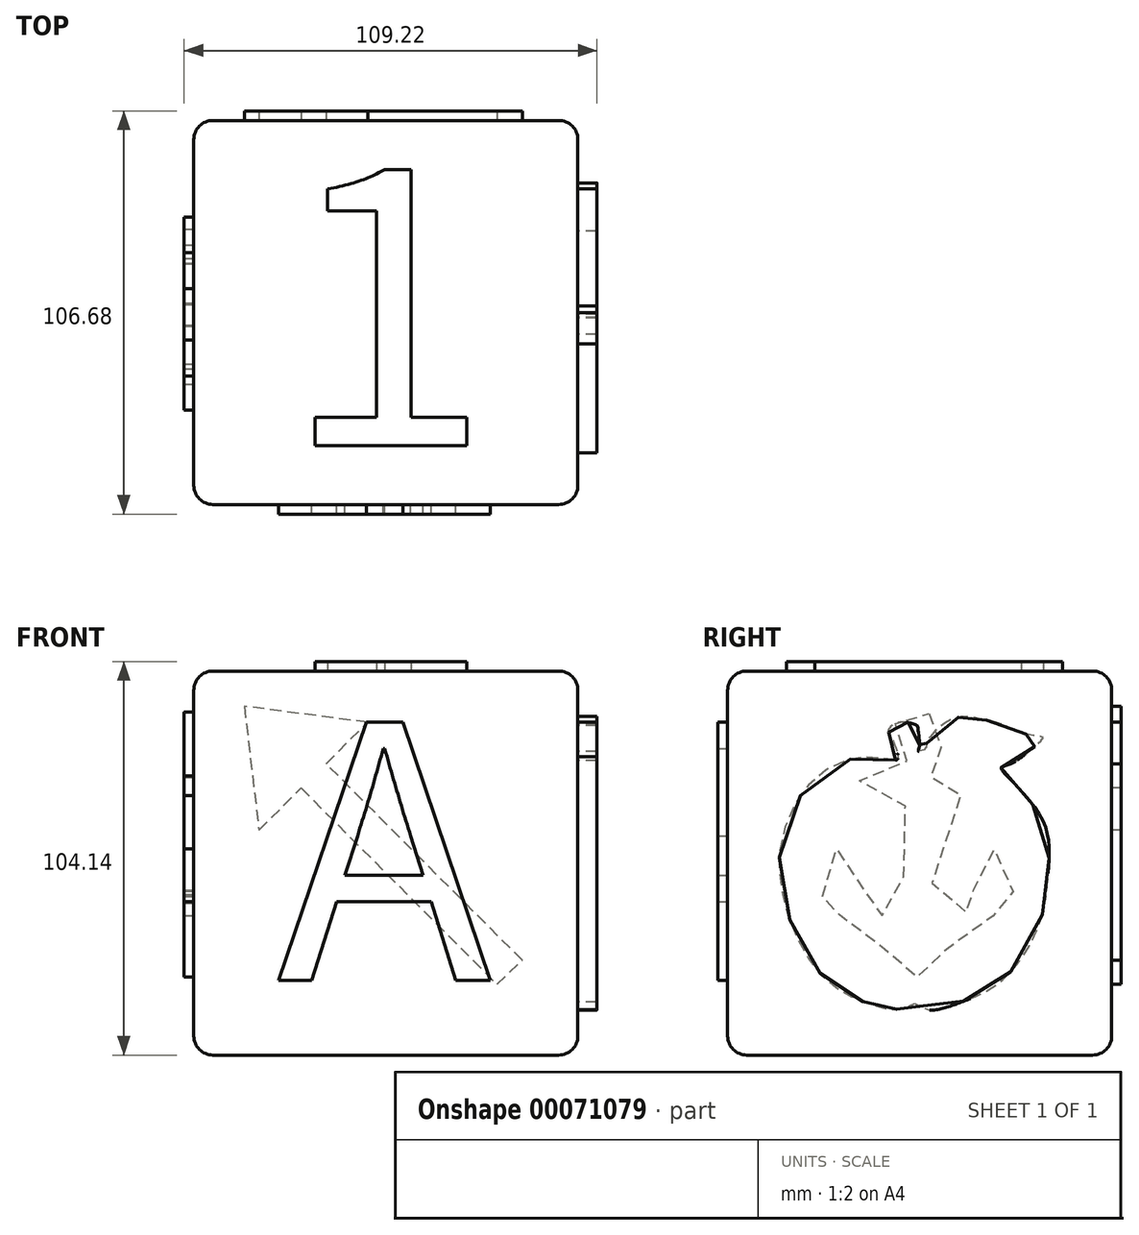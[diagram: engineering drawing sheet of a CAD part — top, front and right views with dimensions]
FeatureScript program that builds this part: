
annotation { "Feature Type Name" : "Feature", "Feature Type Description" : "" }
export const myFeature = defineFeature(function(context is Context, id is Id, definition is map)
    precondition{}
    {
        {
            var Q0;
            Q0=qCreatedBy(makeId("Top.planeOp"),FACE);
            var sketch = newSketch(context, id + "F0", { "sketchPlane" : qUnion([Q0])});
            skLineSegment(sketch, "E0.bottom", {"start": v(-60.77, 32.05) * mm, "end": v(40.83, 32.05) * mm});
            skLineSegment(sketch, "E0.top", {"start": v(-60.77, -69.55) * mm, "end": v(40.83, -69.55) * mm});
            skLineSegment(sketch, "E0.left", {"start": v(-60.77, 32.05) * mm, "end": v(-60.77, -69.55) * mm});
            skLineSegment(sketch, "E0.right", {"start": v(40.83, 32.05) * mm, "end": v(40.83, -69.55) * mm});
            skSolve(sketch);
        }
        {
            var Q0;
            Q0=makeQuery(id+"F0.imprint","IMPRINT",FACE,{"disambiguationData":[TD([[makeQuery(id+"F0.imprint","IMPRINT",EDGE,{"derivedFrom":sQuery(id+"F0.wireOp",EDGE,"E0.bottom")}),-1.0]])]});
            extrude(context, id + "F1", {"entities" : qUnion([Q0]), "depth" : 101.6 * mm});
        }
        {
            var Q0;
            Q0=makeQuery(id+"F1.opExtrude","CAP_EDGE",EDGE,{"disambiguationData":[OSD([sQuery(id+"F0.wireOp",EDGE,"E0.top")])],"isStart":false});
            var Q1;
            Q1=makeQuery(id+"F1.opExtrude","CAP_EDGE",EDGE,{"disambiguationData":[OSD([sQuery(id+"F0.wireOp",EDGE,"E0.right")])],"isStart":false});
            var Q2;
            Q2=makeQuery(id+"F1.opExtrude","CAP_EDGE",EDGE,{"disambiguationData":[OSD([sQuery(id+"F0.wireOp",EDGE,"E0.bottom")])],"isStart":false});
            var Q3;
            Q3=makeQuery(id+"F1.opExtrude","CAP_EDGE",EDGE,{"disambiguationData":[OSD([sQuery(id+"F0.wireOp",EDGE,"E0.left")])],"isStart":false});
            var Q4;
            Q4=makeQuery(id+"F1.opExtrude","SWEPT_EDGE",EDGE,{"disambiguationData":[OSD([sQuery(id+"F0.wireOp",EDGE,"E0.top"),sQuery(id+"F0.wireOp",EDGE,"E0.right")])]});
            var Q5;
            Q5=makeQuery(id+"F1.opExtrude","CAP_EDGE",EDGE,{"disambiguationData":[OSD([sQuery(id+"F0.wireOp",EDGE,"E0.right")])],"isStart":true});
            var Q6;
            Q6=makeQuery(id+"F1.opExtrude","SWEPT_EDGE",EDGE,{"disambiguationData":[OSD([sQuery(id+"F0.wireOp",EDGE,"E0.bottom"),sQuery(id+"F0.wireOp",EDGE,"E0.right")])]});
            var Q7;
            Q7=makeQuery(id+"F1.opExtrude","SWEPT_EDGE",EDGE,{"disambiguationData":[OSD([sQuery(id+"F0.wireOp",EDGE,"E0.top"),sQuery(id+"F0.wireOp",EDGE,"E0.left")])]});
            var Q8;
            Q8=makeQuery(id+"F1.opExtrude","CAP_EDGE",EDGE,{"disambiguationData":[OSD([sQuery(id+"F0.wireOp",EDGE,"E0.top")])],"isStart":true});
            var Q9;
            Q9=makeQuery(id+"F1.opExtrude","SWEPT_EDGE",EDGE,{"disambiguationData":[OSD([sQuery(id+"F0.wireOp",EDGE,"E0.bottom"),sQuery(id+"F0.wireOp",EDGE,"E0.left")])]});
            var Q10;
            Q10=makeQuery(id+"F1.opExtrude","CAP_EDGE",EDGE,{"disambiguationData":[OSD([sQuery(id+"F0.wireOp",EDGE,"E0.bottom")])],"isStart":true});
            var Q11;
            Q11=makeQuery(id+"F1.opExtrude","CAP_EDGE",EDGE,{"disambiguationData":[OSD([sQuery(id+"F0.wireOp",EDGE,"E0.left")])],"isStart":true});
            fillet(context, id + "F2", {"entities" : qUnion([Q0, Q1, Q2, Q3, Q4, Q5, Q6, Q7, Q8, Q9, Q10, Q11]), "radius" : 5.08 * mm, "tangentPropagation" : true, "allowEdgeOverflow" : false});
        }
        {
            var Q0;
            Q0=makeQuery(id+"F1.opExtrude","SWEPT_FACE",FACE,{"disambiguationData":[OSD([sQuery(id+"F0.wireOp",EDGE,"E0.right")])]});
            var sketch = newSketch(context, id + "F3", { "sketchPlane" : qUnion([Q0])});
            skFitSpline(sketch, "E1", {"points": [v(-25.17, 78) * mm, v(-32.49, 78.89) * mm, v(-46.6, 73.07) * mm, v(-55.41, 56.14) * mm, v(-54.09, 38.68) * mm, v(-46.33, 23) * mm, v(-36.9, 15.58) * mm, v(-28.43, 12.41) * mm, v(-25.52, 12.06) * mm, v(-20.06, 13.65) * mm, v(-20.15, 14) * mm, v(-17.68, 12.23) * mm, v(-8.5, 13.73) * mm, v(3.13, 19.9) * mm, v(13.18, 35.51) * mm, v(15.38, 50.41) * mm, v(13.35, 63.02) * mm, v(3.3, 75) * mm, v(2.86, 76.15) * mm, v(5.68, 77.21) * mm, v(13.8, 83.74) * mm, v(13.88, 84.09) * mm, v(9.65, 84.88) * mm, v(1.45, 88.06) * mm, v(-2.78, 88.94) * mm, v(-5.78, 89.62) * mm, v(-11.68, 88.15) * mm, v(-16.97, 82.41) * mm, v(-17.24, 80.92) * mm, v(-19.09, 80.39) * mm, v(-18.91, 81.18) * mm, v(-19.44, 87.26) * mm, v(-19.53, 87.26) * mm, v(-21.56, 87.97) * mm, v(-25.61, 87.53) * mm, v(-27.02, 85.94) * mm, v(-26.76, 85.06) * mm, v(-24.47, 78.98) * mm, v(-25.17, 78) * mm]});
            skSolve(sketch);
        }
        {
            var Q0;
            Q0 = qSketchRegion(id + "F3", true);
            extrude(context, id + "F4", {"entities" : qUnion([Q0]), "operationType" : NewBodyOperationType.ADD, "depth" : 5.08 * mm});
        }
        {
            var Q0;
            Q0=makeQuery(id+"F1.opExtrude","SWEPT_FACE",FACE,{"disambiguationData":[OSD([sQuery(id+"F0.wireOp",EDGE,"E0.left")])]});
            var sketch = newSketch(context, id + "F5", { "sketchPlane" : qUnion([Q0])});
            skPoint(sketch, "E2.107.internal.snap0", {"position": v(19.07, 20.61) * mm});
            skFitSpline(sketch, "E2", {"points": [v(16.32, 90.34) * mm, v(14.88, 89.39) * mm, v(13.13, 86.96) * mm, v(12.61, 85.53) * mm, v(12.54, 83.61) * mm, v(12.81, 82.22) * mm, v(13.73, 80.55) * mm, v(14.93, 79.2) * mm, v(16.05, 78.43) * mm, v(16.56, 78.15) * mm, v(16.56, 77.84) * mm, v(16.45, 73.77) * mm, v(16.4, 73.7) * mm, v(3.25, 73.66) * mm, v(2.93, 73.62) * mm, v(5.8, 69.12) * mm, v(5.8, 68.92) * mm, v(16.05, 68.75) * mm, v(16.17, 68.71) * mm, v(15.42, 45.25) * mm, v(13.07, 38.64) * mm, v(10.72, 37.33) * mm, v(9.48, 36.93) * mm, v(7.01, 37.5) * mm, v(3.42, 40.24) * mm, v(1.75, 42.4) * mm, v(1.07, 43.27) * mm, v(1, 43.59) * mm, v(4.06, 43.59) * mm, v(4.5, 43.75) * mm, v(3.22, 45.06) * mm, v(1.35, 48.1) * mm, v(0, 51.48) * mm, v(-0.89, 53.47) * mm, v(-1.09, 54.86) * mm, v(-2.16, 53.27) * mm, v(-4.12, 49.77) * mm, v(-5.35, 46.58) * mm, v(-6.03, 42.64) * mm, v(-6.42, 40.29) * mm, v(-6.1, 40.49) * mm, v(-3.31, 42.56) * mm, v(-3.27, 42.28) * mm, v(-0.96, 37.3) * mm, v(2.07, 33.47) * mm, v(6.06, 30.56) * mm, v(9.73, 28.69) * mm, v(12.8, 27.45) * mm, v(15.5, 25.54) * mm, v(16.98, 24.46) * mm, v(18.34, 22.55) * mm, v(19.18, 20.95) * mm, v(19.46, 20.61) * mm, v(19.54, 21.03) * mm, v(20.53, 22.46) * mm, v(22.25, 24.46) * mm, v(24.64, 26.45) * mm, v(27.55, 27.88) * mm, v(30.66, 28.87) * mm, v(35.36, 31.82) * mm, v(38.1, 34.24) * mm, v(40.1, 37.5) * mm, v(41.22, 40.7) * mm, v(41.41, 41.93) * mm, v(41.61, 41.7) * mm, v(43.73, 40.81) * mm, v(44.56, 40.57) * mm, v(44.56, 41.29) * mm, v(44.12, 45.67) * mm, v(43.72, 48.78) * mm, v(41.85, 53.12) * mm, v(40.9, 54.4) * mm, v(40.77, 54.6) * mm, v(39.74, 52.13) * mm, v(37.35, 47.95) * mm, v(34.72, 44.64) * mm, v(33.76, 44) * mm, v(33.68, 43.93) * mm, v(37.27, 43.33) * mm, v(37.7, 43.25) * mm, v(34.88, 39.46) * mm, v(29.22, 36.96) * mm, v(25.99, 37.68) * mm, v(23.71, 40.27) * mm, v(23.32, 42.42) * mm, v(23.12, 43.26) * mm, v(22.91, 50.15) * mm, v(22.83, 54.05) * mm, v(22.75, 61.94) * mm, v(22.5, 67.12) * mm, v(22.43, 68.51) * mm, v(22.43, 68.63) * mm, v(32.43, 68.62) * mm, v(32.4, 68.62) * mm, v(35.38, 73.48) * mm, v(35.54, 73.76) * mm, v(22.43, 73.69) * mm, v(22.23, 73.69) * mm, v(22.1, 77.55) * mm, v(22.14, 78.11) * mm, v(23.62, 78.99) * mm, v(25.37, 81.1) * mm, v(26.05, 84.32) * mm, v(25.69, 86.67) * mm, v(23.9, 89.3) * mm, v(21.98, 90.5) * mm, v(20.7, 90.62) * mm, v(19.07, 90.74) * mm, v(17.87, 90.5) * mm, v(16.32, 90.34) * mm]});
            skSolve(sketch);
        }
        {
            var Q0;
            Q0=makeQuery(id+"F5.imprint","IMPRINT",FACE,{"disambiguationData":[TD([[makeQuery(id+"F5.imprint","IMPRINT",EDGE,{"derivedFrom":sQuery(id+"F5.wireOp",EDGE,"E2")}),1.0]])]});
            extrude(context, id + "F6", {"entities" : qUnion([Q0]), "operationType" : NewBodyOperationType.ADD, "depth" : 2.54 * mm});
        }
        {
            var Q0;
            Q0=makeQuery(id+"F1.opExtrude","SWEPT_FACE",FACE,{"disambiguationData":[OSD([sQuery(id+"F0.wireOp",EDGE,"E0.bottom")])]});
            var sketch = newSketch(context, id + "F7", { "sketchPlane" : qUnion([Q0])});
            skLineSegment(sketch, "E3", {"start": v(-26.1, 25.08) * mm, "end": v(25.77, 77.1) * mm});
            skLineSegment(sketch, "E4", {"start": v(25.77, 77.1) * mm, "end": v(14.8, 88.05) * mm});
            skLineSegment(sketch, "E5", {"start": v(14.8, 88.05) * mm, "end": v(47.4, 92.25) * mm});
            skLineSegment(sketch, "E6", {"start": v(47.4, 92.25) * mm, "end": v(43.54, 59.52) * mm});
            skLineSegment(sketch, "E7", {"start": v(43.54, 59.52) * mm, "end": v(32.37, 70.65) * mm});
            skLineSegment(sketch, "E8", {"start": v(32.37, 70.65) * mm, "end": v(-19.38, 18.75) * mm});
            skLineSegment(sketch, "E9", {"start": v(-19.38, 18.75) * mm, "end": v(-26.1, 25.08) * mm});
            skSolve(sketch);
        }
        {
            var Q0;
            Q0 = qSketchRegion(id + "F7", true);
            extrude(context, id + "F8", {"entities" : qUnion([Q0]), "operationType" : NewBodyOperationType.ADD, "depth" : 2.54 * mm});
        }
        {
            var Q0;
            Q0=makeQuery(id+"F1.opExtrude","SWEPT_FACE",FACE,{"disambiguationData":[OSD([sQuery(id+"F0.wireOp",EDGE,"E0.top")])]});
            var sketch = newSketch(context, id + "F9", { "sketchPlane" : qUnion([Q0])});
            skText(sketch, "E10", { "text": "A", "fontName": "NotoSansCJKtc-Regular.otf"});
            const initialGuessF9  = {"E10": [-0.03864, 0.01974, 1, 0, 0.06717]};
            skSetInitialGuess(sketch, initialGuessF9);
            skSolve(sketch);
        }
        {
            var Q0;
            Q0 = qSketchRegion(id + "F9", true);
            extrude(context, id + "F10", {"entities" : qUnion([Q0]), "operationType" : NewBodyOperationType.ADD, "depth" : 2.54 * mm});
        }
        {
            var Q0;
            Q0=makeQuery(id+"F1.opExtrude","CAP_FACE",FACE,{"disambiguationData":[OSD([sQuery(id+"F0.wireOp",EDGE,"E0.bottom"),sQuery(id+"F0.wireOp",EDGE,"E0.top"),sQuery(id+"F0.wireOp",EDGE,"E0.left"),sQuery(id+"F0.wireOp",EDGE,"E0.right")])],"isStart":false});
            var sketch = newSketch(context, id + "F11", { "sketchPlane" : qUnion([Q0])});
            skText(sketch, "E11", { "text": "1", "fontName": "NotoSansCJKsc-Regular.otf"});
            const initialGuessF11  = {"E11": [-0.03745, -0.05401, 1, 0, 0.0718]};
            skSetInitialGuess(sketch, initialGuessF11);
            skSolve(sketch);
        }
        {
            var Q0;
            Q0 = qSketchRegion(id + "F11", true);
            extrude(context, id + "F12", {"entities" : qUnion([Q0]), "operationType" : NewBodyOperationType.ADD, "depth" : 2.54 * mm});
        }
    });
